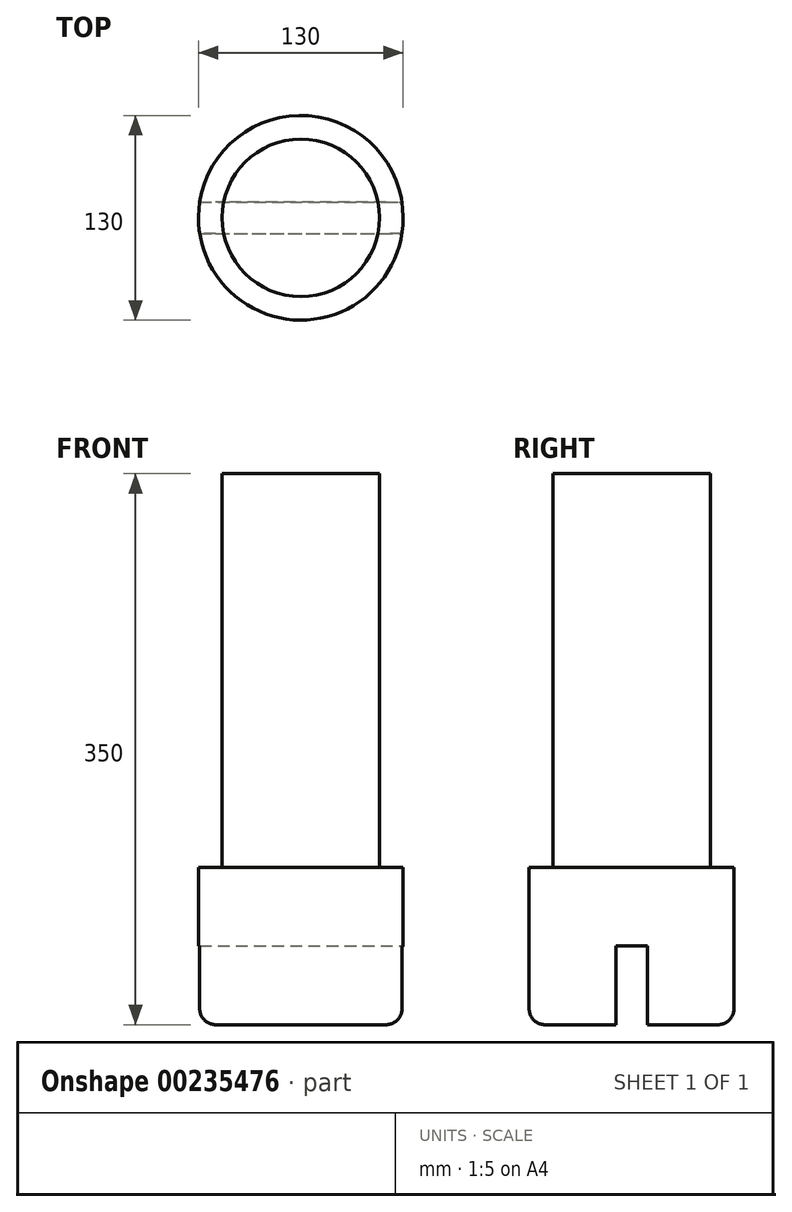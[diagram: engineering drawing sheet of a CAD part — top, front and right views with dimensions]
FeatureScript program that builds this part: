
annotation { "Feature Type Name" : "Feature", "Feature Type Description" : "" }
export const myFeature = defineFeature(function(context is Context, id is Id, definition is map)
    precondition{}
    {
        {
            var Q0;
            Q0=qCreatedBy(makeId("Top.planeOp"),FACE);
            var sketch = newSketch(context, id + "F0", { "sketchPlane" : qUnion([Q0])});
            skCircle(sketch, "E0", {"center": v(0, 0) * mm, "radius": 65 * mm});
            skCircle(sketch, "E1", {"center": v(0, 0) * mm, "radius": 50 * mm});
            skSolve(sketch);
        }
        {
            var Q0;
            Q0=makeQuery(id+"F0.imprint","IMPRINT",FACE,{"disambiguationData":[TD([[makeQuery(id+"F0.imprint","IMPRINT",EDGE,{"derivedFrom":sQuery(id+"F0.wireOp",EDGE,"E1")}),1.0]])]});
            extrude(context, id + "F1", {"entities" : qUnion([Q0]), "depth" : 350 * mm});
        }
        {
            var Q0;
            Q0=makeQuery(id+"F0.imprint","IMPRINT",FACE,{"disambiguationData":[TD([[makeQuery(id+"F0.imprint","IMPRINT",EDGE,{"derivedFrom":sQuery(id+"F0.wireOp",EDGE,"E0")}),1.0]])]});
            extrude(context, id + "F2", {"entities" : qUnion([Q0]), "operationType" : NewBodyOperationType.ADD, "depth" : 100 * mm});
        }
        {
            var Q0;
            Q0=makeQuery(id+"F2.opExtrude","CAP_EDGE",EDGE,{"disambiguationData":[OSD([sQuery(id+"F0.wireOp",EDGE,"E0")])],"isStart":true});
            fillet(context, id + "F3", {"entities" : qUnion([Q0]), "radius" : 10 * mm, "tangentPropagation" : true, "allowEdgeOverflow" : false});
        }
        {
            var Q0;
            Q0=qCreatedBy(makeId("Right.planeOp"),FACE);
            var sketch = newSketch(context, id + "F4", { "sketchPlane" : qUnion([Q0])});
            skLineSegment(sketch, "E2", {"start": v(10, -3.73) * mm, "end": v(10, 50) * mm});
            skLineSegment(sketch, "E3", {"start": v(10, 50) * mm, "end": v(-10, 50) * mm});
            skLineSegment(sketch, "E4", {"start": v(-10, 50) * mm, "end": v(-10, -3.73) * mm});
            skLineSegment(sketch, "E5", {"start": v(-10, -3.73) * mm, "end": v(10, -3.73) * mm});
            skSolve(sketch);
        }
        {
            var Q0;
            Q0=makeQuery(id+"F4.imprint","IMPRINT",FACE,{"disambiguationData":[TD([[makeQuery(id+"F4.imprint","IMPRINT",EDGE,{"derivedFrom":sQuery(id+"F4.wireOp",EDGE,"E2")}),1.0]])]});
            extrude(context, id + "F5", {"entities" : qUnion([Q0]), "operationType" : NewBodyOperationType.REMOVE, "endBound" : BoundingType.SYMMETRIC, "oppositeDirection" : true, "depth" : 300 * mm});
        }
    });
